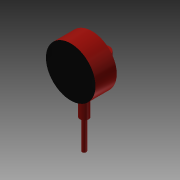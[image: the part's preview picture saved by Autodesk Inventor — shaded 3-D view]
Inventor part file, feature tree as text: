
AUTODESK INVENTOR PART (.ipt)
format: ipt  version: 2014 (Build 180170000, 170)  size: 117,760 bytes
history: native  units: mm
features: extrude x4, sketch x4, other x2, plane x1, projected_geometry x1
ambient origin geometry x8: Origin, YZ Plane, XZ Plane, XY Plane, X Axis, Y Axis, Z Axis, Center Point
bodies: Solid1 (feature_tree)
feature tree (12):
  extrude  "Extrusion1"  Depth=17.0mm
  extrude  "Extrusion2"  Depth=6.5mm TaperAngle=0.0deg
  extrude  "Extrusion3"  Depth=23.0mm TaperAngle=0.0deg
  extrude  "Extrusion4"  Depth=32.0mm
  plane  "Work Plane1"
  sketch  "Sketch2"  dims[d0=6.3mm d1=17.0mm]
  sketch  "Sketch3"  dims[d2=18.65mm d3=6.5mm d4=0.0mm]
  sketch  "Sketch4"  dims[d5=53.4mm d6=23.0mm d7=0.0mm]
  sketch  "Sketch5"  dims[d8=9.52mm d9=8.35mm d10=46.0mm d11=0.0mm d12=4.5mm d13=32.0mm d14=0.0mm]
  other  "Work Axis1"
  other  "Work Point1"
  projected_geometry  "Project Cut Edges1"
